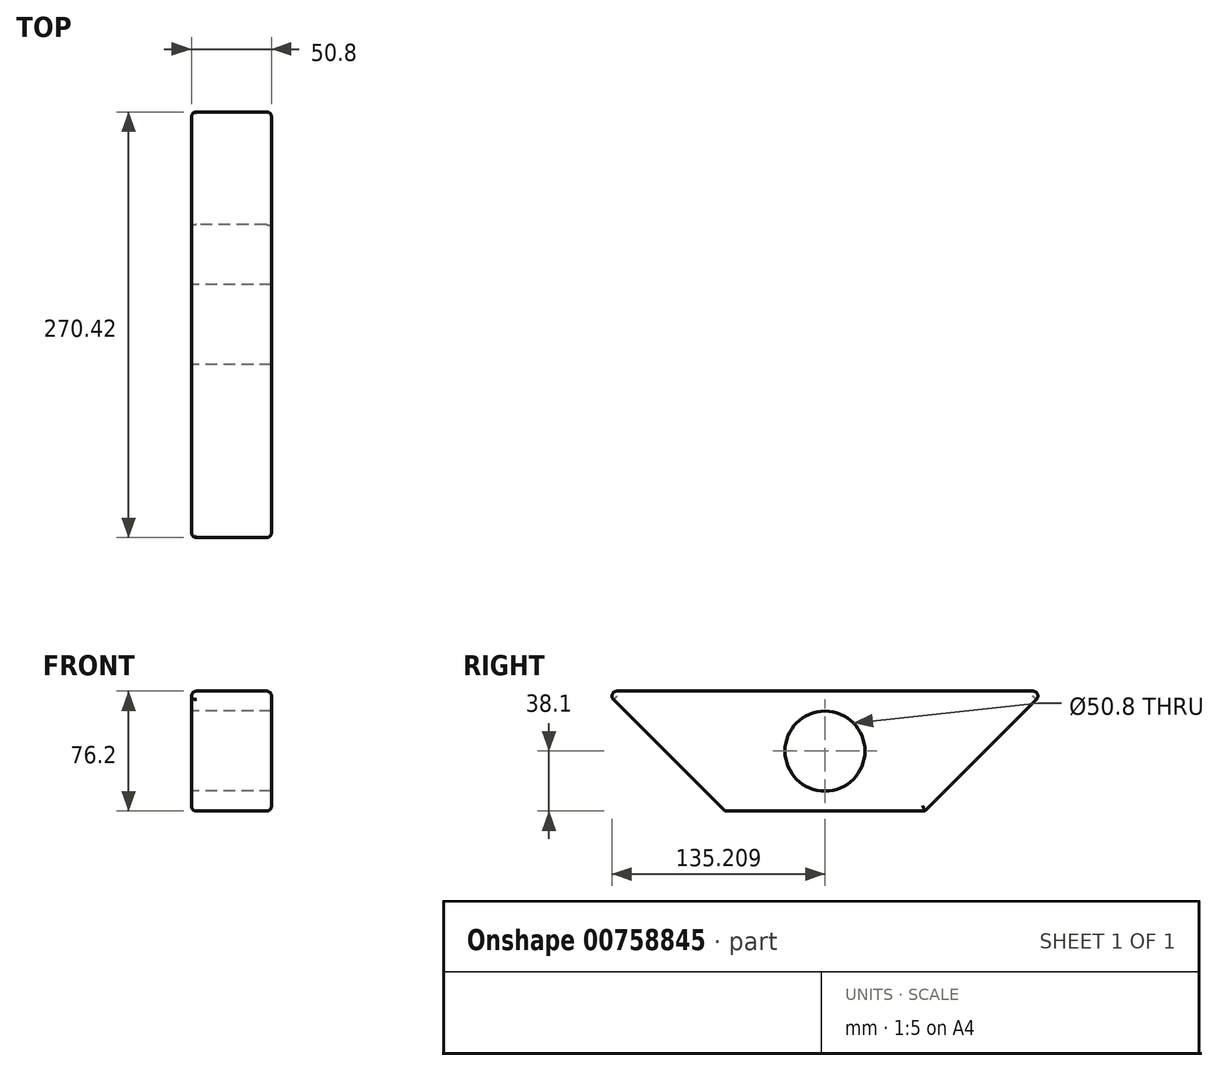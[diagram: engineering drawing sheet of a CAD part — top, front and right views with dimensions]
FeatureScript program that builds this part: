
annotation { "Feature Type Name" : "Feature", "Feature Type Description" : "" }
export const myFeature = defineFeature(function(context is Context, id is Id, definition is map)
    precondition{}
    {
        {
            var Q0;
            Q0=qCreatedBy(makeId("Right.planeOp"),FACE);
            var sketch = newSketch(context, id + "F0", { "sketchPlane" : qUnion([Q0])});
            skLineSegment(sketch, "E0", {"start": v(-70.82, 38.1) * mm, "end": v(208.58, 38.1) * mm});
            skLineSegment(sketch, "E1", {"start": v(208.58, 38.1) * mm, "end": v(132.38, -38.1) * mm});
            skLineSegment(sketch, "E2", {"start": v(132.38, -38.1) * mm, "end": v(5.38, -38.1) * mm});
            skLineSegment(sketch, "E3", {"start": v(5.38, -38.1) * mm, "end": v(-70.82, 38.1) * mm});
            skPoint(sketch, "E4", {"position": v(34.91, 0) * mm});
            skPoint(sketch, "E5", {"position": v(68.88, 0) * mm});
            skPoint(sketch, "E5.positionSnap0", {"position": v(68.88, -38.1) * mm});
            skSolve(sketch);
        }
        {
            var Q0;
            Q0 = qSketchRegion(id + "F0", true);
            extrude(context, id + "F1", {"entities" : qUnion([Q0]), "depth" : 50.8 * mm, "offsetDistance" : 25.4 * mm});
        }
        {
            var Q0;
            Q0=makeQuery(id+"F1.opExtrude","CAP_EDGE",EDGE,{"disambiguationData":[OSD([sQuery(id+"F0.wireOp",EDGE,"E3")])],"isStart":false});
            var Q1;
            Q1=makeQuery(id+"F1.opExtrude","CAP_EDGE",EDGE,{"disambiguationData":[OSD([sQuery(id+"F0.wireOp",EDGE,"E3")])],"isStart":true});
            var Q2;
            Q2=makeQuery(id+"F1.opExtrude","CAP_EDGE",EDGE,{"disambiguationData":[OSD([sQuery(id+"F0.wireOp",EDGE,"E2")])],"isStart":false});
            var Q3;
            Q3=makeQuery(id+"F1.opExtrude","CAP_EDGE",EDGE,{"disambiguationData":[OSD([sQuery(id+"F0.wireOp",EDGE,"E0")])],"isStart":false});
            var Q4;
            Q4=makeQuery(id+"F1.opExtrude","CAP_EDGE",EDGE,{"disambiguationData":[OSD([sQuery(id+"F0.wireOp",EDGE,"E1")])],"isStart":false});
            var Q5;
            Q5=makeQuery(id+"F1.opExtrude","SWEPT_FACE",FACE,{"disambiguationData":[OSD([sQuery(id+"F0.wireOp",EDGE,"E3")])]});
            var Q6;
            Q6=makeQuery(id+"F1.opExtrude","SWEPT_EDGE",EDGE,{"disambiguationData":[OSD([sQuery(id+"F0.wireOp",EDGE,"E2"),sQuery(id+"F0.wireOp",EDGE,"E3")])]});
            var Q7;
            Q7=makeQuery(id+"F1.opExtrude","CAP_EDGE",EDGE,{"disambiguationData":[OSD([sQuery(id+"F0.wireOp",EDGE,"E1")])],"isStart":true});
            var Q8;
            Q8=makeQuery(id+"F1.opExtrude","CAP_EDGE",EDGE,{"disambiguationData":[OSD([sQuery(id+"F0.wireOp",EDGE,"E2")])],"isStart":true});
            var Q9;
            Q9=makeQuery(id+"F1.opExtrude","SWEPT_EDGE",EDGE,{"disambiguationData":[OSD([sQuery(id+"F0.wireOp",EDGE,"E0"),sQuery(id+"F0.wireOp",EDGE,"E1")])]});
            fillet(context, id + "F2", {"entities" : qUnion([Q0, Q1, Q2, Q3, Q4, Q5, Q6, Q7, Q8, Q9]), "radius" : 3.17 * mm, "tangentPropagation" : true, "allowEdgeOverflow" : false});
        }
        {
            var Q0;
            Q0=sQuery(id+"F0.wireOp",VERTEX,"E5");
            var Q1;
            Q1=makeQuery(id+"F1.opExtrude","SWEPT_BODY",BODY,{"disambiguationData":[OSD([sQuery(id+"F0.wireOp",EDGE,"E0"),sQuery(id+"F0.wireOp",EDGE,"E1"),sQuery(id+"F0.wireOp",EDGE,"E2"),sQuery(id+"F0.wireOp",EDGE,"E3")])]});
            hole(context, id + "F3", {"style" : HoleStyle.SIMPLE, "endStyle" : HoleEndStyle.THROUGH, "oppositeDirection" : true, "holeDiameter" : 50.8 * mm, "majorDiameter" : 6.35 * mm, "tappedDepth" : 110.49 * mm, "tapClearance" : 3, "startFromSketch" : true, "locations" : qUnion([Q0]), "scope" : qUnion([Q1])});
        }
        {
            var Q0;
            Q0=makeQuery(id+"F1.opExtrude","CAP_EDGE",EDGE,{"disambiguationData":[OSD([sQuery(id+"F0.wireOp",EDGE,"E0")])],"isStart":true});
            fillet(context, id + "F4", {"entities" : qUnion([Q0]), "radius" : 3.17 * mm, "tangentPropagation" : true, "allowEdgeOverflow" : false});
        }
    });
